# Revit family: Überspannungsableiter V20, 2-polig
name_source: partatom
category: Generic Models
revit_build: Autodesk Revit 2015 (Build: 20140606_1530(x64)
units: mm (PartAtom-declared; Revit-internal decimal feet)

## types (5) — shared parameters
Height = 79 mm
Length = 36 mm
Manufacturer = OBO Bettermann
Material = PA 66/6 FR HF RAL 9010
Material 2 = PA 66/6 FR HF RAL 2003
URL = http://www.obo-bettermann.com
Width = 90 mm  [stored 0.295276 ft]

## per-type parameters (varying)
| type | Article Type | GTIN | Manufacturer Art.No. |
| V20-2-75 | V20-2-75 | 4012196159741 | 5095142 |
| v20-2-150 | V20-2-150 | 4012196159772 | 5095152 |
| v20-2-280 | V20-2-280 | 4012196159819 | 5095162 |
| v20-2-385 | V20-2-385 | 4012196159895 | 5095192 |
| v20-2-550 | V20-2-550 | 4012196159963 | 5095212 |

note: [stored X ft] marks values corroborated as IEEE doubles in the binary element streams (Revit-internal decimal feet)

## geometry (parser evidence)
native form markers: Sweep x2
no freeform markers — native parametric forms only
